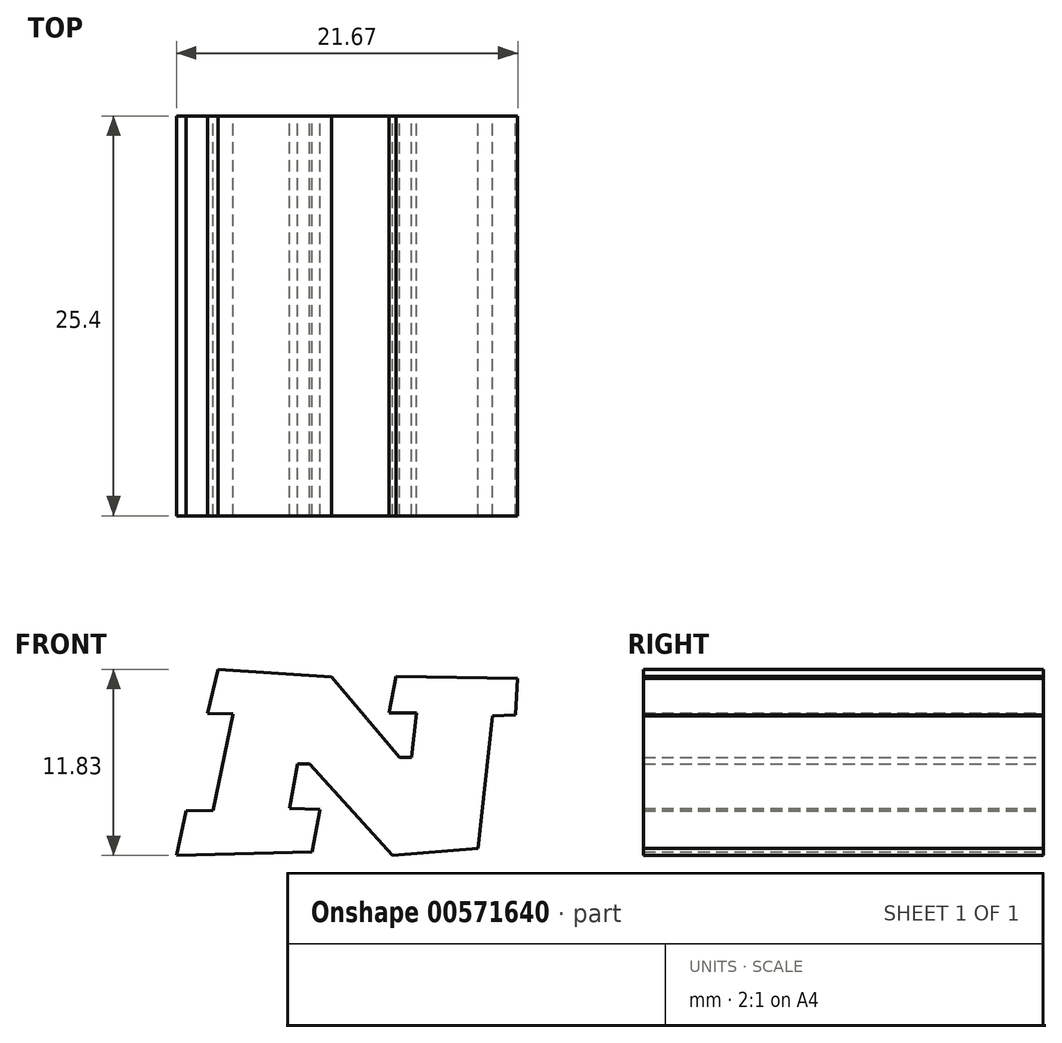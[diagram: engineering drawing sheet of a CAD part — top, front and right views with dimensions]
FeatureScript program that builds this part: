
annotation { "Feature Type Name" : "Feature", "Feature Type Description" : "" }
export const myFeature = defineFeature(function(context is Context, id is Id, definition is map)
    precondition{}
    {
        {
            var Q0;
            Q0=qCreatedBy(makeId("Front.planeOp"),FACE);
            var sketch = newSketch(context, id + "F0", { "sketchPlane" : qUnion([Q0])});
            skFitSpline(sketch, "E0", {"points": [v(-58.4, 49.98) * mm, v(-60.28, 49.9) * mm, v(-62.5, 51.34) * mm, v(-63.35, 53.39) * mm, v(-63.35, 56.37) * mm, v(-62.67, 59.19) * mm, v(-61.05, 62.26) * mm, v(-58.92, 64.47) * mm, v(-56.27, 66.35) * mm, v(-53.29, 67.46) * mm, v(-49.88, 67.88) * mm, v(-46.55, 67.88) * mm, v(-44.42, 67.46) * mm, v(-42.2, 66.1) * mm, v(-40.24, 64.39) * mm, v(-38.7, 62.6) * mm, v(-37.68, 60.38) * mm, v(-36.06, 58.33) * mm, v(-34.7, 56.2) * mm, v(-33.93, 54.15) * mm, v(-33.25, 50.91) * mm, v(-32.4, 53.64) * mm, v(-31.37, 56.46) * mm, v(-30.43, 59.1) * mm, v(-29.58, 61.23) * mm, v(-28.39, 63.1) * mm, v(-25.66, 64.9) * mm, v(-22.93, 65.07) * mm, v(-20.63, 65.15) * mm, v(-17.47, 64.9) * mm, v(-14.66, 63.7) * mm, v(-14.15, 60.64) * mm, v(-14.66, 59.19) * mm, v(-12.78, 58.84) * mm, v(-10.48, 56.88) * mm, v(-11.33, 53.56) * mm, v(-12.87, 49.2) * mm, v(-14.91, 43.5) * mm, v(-14.49, 43.5) * mm, v(-11.16, 44.86) * mm, v(-6.73, 45.29) * mm, v(-3.15, 44.69) * mm, v(-1.1, 43.58) * mm, v(1.03, 41.1) * mm, v(2.4, 38.3) * mm, v(2.74, 38.9) * mm, v(3.67, 41.53) * mm, v(5.12, 45.37) * mm, v(11.33, 58.89) * mm], "startDerivative": vector(-109.1, -22.32) * mm, "endDerivative": vector(157.1, 333.02) * mm});
            skFitSpline(sketch, "E1", {"points": [v(9.15, 54.27) * mm, v(9.8, 55.46) * mm, v(10.82, 57.18) * mm, v(12.5, 59.97) * mm, v(14.65, 63.06) * mm, v(17.43, 66.2) * mm, v(20.08, 68) * mm, v(22.91, 69.14) * mm, v(25.96, 69.71) * mm, v(29.37, 69.64) * mm, v(32.92, 68.7) * mm, v(35.28, 67.2) * mm, v(36.24, 65.83) * mm, v(36.87, 64.39) * mm, v(37.18, 62.64) * mm, v(38.47, 61.88) * mm, v(39.59, 60.43) * mm, v(40.27, 58.71) * mm, v(40.37, 55.21) * mm, v(39.94, 53.4) * mm, v(38.55, 49.76) * mm, v(37.52, 47.71) * mm, v(36.35, 45.4) * mm, v(36.59, 45.36) * mm, v(37.92, 45.3) * mm, v(39.85, 44.97) * mm, v(41.44, 44.4) * mm, v(43.55, 43) * mm, v(43.77, 43.1) * mm, v(44.76, 43.85) * mm, v(46.5, 44.76) * mm, v(48.74, 45.2) * mm, v(50.73, 45.09) * mm, v(52.45, 44.03) * mm, v(53.32, 42.47) * mm, v(53.56, 39.4) * mm, v(53.97, 39.41) * mm, v(55.66, 38.75) * mm, v(56.74, 37.12) * mm, v(56.92, 34.7) * mm, v(56.08, 31.7) * mm, v(54.87, 28.86) * mm, v(53.18, 24.76) * mm, v(53.73, 24.82) * mm, v(55.78, 25.3) * mm, v(58.8, 25.36) * mm, v(62.23, 24.46) * mm, v(65.12, 22.9) * mm, v(67.23, 20.48) * mm, v(68.44, 18.61) * mm, v(68.95, 16.93) * mm, v(70.23, 15.82) * mm, v(72.19, 12.41) * mm, v(72.87, 9.09) * mm, v(72.95, 2.44) * mm, v(71.67, -3.28) * mm, v(68.99, -8.5) * mm, v(66.68, -11.44) * mm, v(64.72, -13.53) * mm, v(56.88, -18.9) * mm, v(51.51, -20.88) * mm, v(46.03, -22.2) * mm, v(39.34, -23.11) * mm, v(31.89, -23.82) * mm, v(13.7, -24.56) * mm, v(1.77, -25.4) * mm, v(-17.72, -27.26) * mm, v(-35.46, -30.33) * mm, v(-53.03, -34.33) * mm, v(-62.82, -36.78) * mm, v(-66.48, -35.67) * mm, v(-66.37, -32.52) * mm, v(-66.93, -32.47) * mm, v(-69.62, -32.32) * mm, v(-71.2, -30.9) * mm, v(-71.65, -28.37) * mm, v(-70.63, -25.22) * mm, v(-68.66, -20.6) * mm, v(-65.87, -13.91) * mm, v(-60.27, -1.04) * mm, v(-58.65, 2.45) * mm, v(-55.58, 4.59) * mm, v(-50.42, 5.35) * mm, v(-43.1, 5.7) * mm, v(-36.61, 5.82) * mm, v(-29.32, 5.7) * mm, v(-19.9, 5.57) * mm, v(1.25, 3.91) * mm, v(12.53, 2.83) * mm, v(22.12, 2.04) * mm, v(30.27, 1.6) * mm, v(38.2, 1.43) * mm, v(45.2, 2.7) * mm, v(51.34, 4.41) * mm, v(55.86, 8.76) * mm, v(54.58, 8) * mm, v(50.23, 5.52) * mm, v(43.66, 4.33) * mm, v(40.42, 5.7) * mm, v(39.14, 8) * mm, v(37.6, 6.8) * mm, v(33.86, 4.76) * mm, v(28.65, 4.16) * mm, v(24.73, 6.38) * mm, v(23.2, 8.68) * mm, v(22, 8) * mm, v(16.97, 5.44) * mm, v(11.86, 4.33) * mm, v(7.25, 4.76) * mm, v(3.16, 8.68) * mm, v(2.48, 8.25) * mm, v(-1.53, 6.03) * mm, v(-5.71, 4.67) * mm], "startDerivative": vector(118.95, 221.72) * mm, "endDerivative": vector(-425.56, -118.04) * mm});
            skFitSpline(sketch, "E2", {"points": [v(-25.4, 6.03) * mm, v(-24.27, 6.45) * mm, v(-22.56, 7.45) * mm, v(-20.6, 8.96) * mm, v(-20.45, 8.84) * mm, v(-19.72, 8) * mm, v(-18.28, 6.85) * mm, v(-15.81, 5.34) * mm], "startDerivative": vector(8.64, 3.07) * mm, "endDerivative": vector(13.18, -8.38) * mm});
            skFitSpline(sketch, "E3", {"points": [v(-25.4, 6.03) * mm, v(-25.4, 5.69) * mm], "startDerivative": vector(0, -0.34) * mm, "endDerivative": vector(0, -0.34) * mm});
            skFitSpline(sketch, "E4", {"points": [v(-42.66, 6.03) * mm, v(-41.59, 6.58) * mm, v(-39.9, 7.7) * mm, v(-38.56, 8.62) * mm, v(-38.48, 8.43) * mm, v(-37.62, 7.31) * mm, v(-36.44, 6.03) * mm, v(-36.42, 5.82) * mm], "startDerivative": vector(6.87, 3.3) * mm, "endDerivative": vector(-0.7, -3.13) * mm});
            skFitSpline(sketch, "E5", {"points": [v(-42.66, 6.04) * mm, v(-42.66, 5.82) * mm, v(-42.66, 5.71) * mm], "startDerivative": vector(0, -0.32) * mm, "endDerivative": vector(0, -0.24) * mm});
            skFitSpline(sketch, "E6", {"points": [v(-53.48, 5.28) * mm, v(-54.72, 6.03) * mm, v(-56.42, 7.6) * mm, v(-57.8, 9.4) * mm, v(-58.54, 9.76) * mm, v(-60.31, 11.28) * mm, v(-61.91, 12.9) * mm, v(-63.15, 14.8) * mm, v(-63.81, 16.88) * mm, v(-64.22, 19.11) * mm, v(-64.12, 22.7) * mm, v(-63.36, 25.85) * mm, v(-62.72, 28.38) * mm, v(-61.73, 31.07) * mm, v(-60.92, 33.5) * mm, v(-55.8, 45.72) * mm, v(-56.22, 45.89) * mm, v(-58.01, 47.3) * mm, v(-58.4, 49.98) * mm], "startDerivative": vector(-28.66, 16) * mm, "endDerivative": vector(1.9, 49.58) * mm});
            skFitSpline(sketch, "E7", {"points": [v(16.22, 39.93) * mm, v(17.3, 41.18) * mm, v(18.94, 43.5) * mm, v(20.77, 45.91) * mm, v(22.35, 48.31) * mm, v(25.07, 52.98) * mm, v(27.26, 57) * mm, v(28.55, 59.21) * mm, v(28.98, 61.47) * mm, v(28.48, 61.22) * mm, v(26.9, 59.54) * mm, v(24.64, 56.42) * mm, v(22.78, 53.55) * mm, v(21.02, 50.54) * mm, v(18.83, 46.16) * mm, v(16.22, 39.93) * mm]});
            skFitSpline(sketch, "E8", {"points": [v(30.45, 19.02) * mm, v(31.23, 19.2) * mm, v(32.92, 20.95) * mm, v(34.37, 23.54) * mm, v(35.63, 26.43) * mm, v(36.9, 29.27) * mm, v(38.2, 33.3) * mm, v(38.77, 36.44) * mm, v(37.38, 37.29) * mm, v(35.15, 36.32) * mm, v(33.58, 34.7) * mm, v(31.9, 33) * mm, v(30.63, 30.72) * mm, v(29.24, 28.38) * mm, v(28.46, 25.1) * mm, v(28.28, 22.76) * mm, v(29.48, 19.38) * mm, v(30.45, 19.02) * mm]});
            skFitSpline(sketch, "E9", {"points": [v(-59.75, 51.85) * mm, v(-60.76, 52.42) * mm, v(-61.37, 53.68) * mm, v(-61.33, 55.54) * mm, v(-60.58, 58.41) * mm, v(-59.54, 60.74) * mm, v(-57.64, 62.82) * mm, v(-55.13, 64.65) * mm, v(-52.05, 65.69) * mm, v(-48.68, 66.01) * mm, v(-45.92, 65.69) * mm, v(-43.26, 64.54) * mm, v(-41.07, 62.64) * mm, v(-39.57, 60.06) * mm, v(-38.85, 57.62) * mm, v(-38.92, 54.07) * mm, v(-39.93, 50.6) * mm, v(-41, 47.58) * mm, v(-42.35, 44.22) * mm, v(-48.08, 30.43) * mm, v(-49.36, 27.36) * mm, v(-50.12, 24.12) * mm, v(-49.95, 20.02) * mm, v(-48.08, 18.57) * mm, v(-45.1, 18.66) * mm, v(-42.79, 21.73) * mm, v(-39.63, 27.87) * mm, v(-37.25, 34.1) * mm, v(-35.29, 39.41) * mm, v(-31.96, 49.1) * mm, v(-28.04, 59.5) * mm, v(-26.33, 62.06) * mm, v(-22.58, 63.17) * mm, v(-19.08, 63) * mm, v(-16.61, 62.49) * mm, v(-16.18, 60.78) * mm, v(-17.55, 56.26) * mm, v(-19.5, 51.23) * mm, v(-21.13, 46.29) * mm, v(-23.1, 40.92) * mm, v(-25.05, 36.32) * mm, v(-27.78, 29.23) * mm, v(-29.4, 25.14) * mm, v(-30.77, 21.81) * mm, v(-31.1, 19) * mm, v(-29.32, 18.66) * mm, v(-27.36, 20.02) * mm, v(-25.73, 22.07) * mm, v(-25.22, 25.9) * mm, v(-23.18, 31.02) * mm, v(-21.22, 34.95) * mm, v(-18.15, 38.53) * mm, v(-15.16, 40.92) * mm, v(-10.73, 42.88) * mm, v(-7.4, 43.47) * mm, v(-3.73, 42.8) * mm, v(0, 39.41) * mm, v(0, 34.95) * mm, v(-1.77, 31.2) * mm, v(-4.93, 29.66) * mm, v(-8.22, 30.18) * mm, v(-9.26, 31) * mm, v(-10.01, 32.58) * mm, v(-9.87, 33.87) * mm, v(-9.26, 35.09) * mm, v(-8.43, 35.99) * mm, v(-7.47, 36.32) * mm, v(-6.68, 36.32) * mm, v(-5.35, 36.32) * mm, v(-5.53, 37.06) * mm, v(-6, 37.67) * mm, v(-7.44, 38.08) * mm, v(-9.11, 37.55) * mm, v(-11.52, 35.9) * mm, v(-12.74, 34.46) * mm, v(-13.86, 32.78) * mm, v(-16.05, 27.87) * mm, v(-16.31, 25.1) * mm, v(-16.01, 21.82) * mm, v(-14.9, 19.86) * mm, v(-12.18, 18.57) * mm, v(-9.17, 18.46) * mm, v(-6.77, 19.2) * mm, v(-4.3, 20.07) * mm, v(-0.6, 22.22) * mm, v(0.5, 25.77) * mm, v(1.51, 29.14) * mm, v(2.73, 32.76) * mm, v(3.95, 36.32) * mm, v(5.25, 40.24) * mm, v(8.27, 47.95) * mm, v(10.24, 52.16) * mm, v(13.08, 57.08) * mm, v(16.12, 61.64) * mm, v(18.98, 64.84) * mm, v(22.68, 66.97) * mm, v(26.18, 67.73) * mm, v(29.78, 67.42) * mm, v(33.22, 66.3) * mm, v(35.15, 63.26) * mm, v(34.54, 58.35) * mm, v(32.87, 54.44) * mm, v(31.23, 51.45) * mm, v(29.93, 48.76) * mm, v(28.3, 46.13) * mm, v(21.52, 36.95) * mm, v(19.23, 34.66) * mm, v(16.63, 31.88) * mm, v(13.7, 28.8) * mm, v(10.48, 25.85) * mm, v(10.42, 25.13) * mm, v(9.52, 22.12) * mm, v(9.7, 19.2) * mm, v(11.27, 18.26) * mm, v(14.76, 19.2) * mm, v(18.74, 21.75) * mm, v(18.86, 22.48) * mm, v(18.92, 24.47) * mm, v(19.29, 26.64) * mm, v(20.25, 28.99) * mm, v(21.82, 33.21) * mm, v(23.8, 36.32) * mm, v(26.28, 38.76) * mm, v(29.48, 41.17) * mm, v(32.85, 42.68) * mm, v(35.69, 43.34) * mm, v(37.92, 43.34) * mm, v(40.45, 42.74) * mm, v(43.35, 39.96) * mm, v(43.83, 40.5) * mm, v(45.82, 42.13) * mm, v(47.69, 42.86) * mm, v(49.8, 43.22) * mm, v(51.55, 42.01) * mm, v(51.67, 40.02) * mm, v(51, 37.67) * mm, v(49.86, 35.02) * mm, v(48.65, 31.7) * mm, v(47.32, 28.63) * mm, v(45.46, 23.62) * mm, v(44.43, 20.55) * mm, v(44.5, 19.2) * mm, v(45.58, 18.02) * mm, v(48.23, 19.2) * mm, v(51.24, 21.63) * mm, v(54.98, 23.08) * mm, v(58.54, 23.38) * mm, v(62.16, 22.36) * mm, v(65.35, 19.95) * mm, v(67.1, 16.63) * mm, v(67.73, 11.37) * mm, v(67.51, 6.85) * mm, v(66.68, 2.73) * mm, v(64.36, -1.93) * mm, v(60.99, -6.52) * mm, v(55.9, -10.68) * mm, v(51.38, -13.19) * mm, v(45.94, -15.13) * mm, v(41.12, -16.16) * mm, v(35.15, -16.92) * mm, v(30.85, -17.3) * mm, v(25.56, -17.7) * mm, v(4.96, -18.64) * mm, v(-3.82, -19.28) * mm, v(-8.98, -19.71) * mm, v(-35.46, -23.11) * mm, v(-48.27, -25.9) * mm, v(-57.09, -28.13) * mm, v(-65.2, -30.33) * mm, v(-67.62, -30.33) * mm, v(-69.49, -29.84) * mm, v(-69.56, -28.05) * mm, v(-68.48, -25.43) * mm, v(-67.3, -22.57) * mm, v(-65.94, -19.2) * mm, v(-64.58, -16.18) * mm, v(-63.18, -12.6) * mm, v(-61.24, -8.5) * mm, v(-58.65, -2.15) * mm, v(-57.18, 1.05) * mm, v(-55.8, 2.45) * mm, v(-53.63, 3.23) * mm, v(-50.6, 3.58) * mm, v(-46.43, 3.74) * mm, v(-42.58, 3.89) * mm, v(-23.57, 3.89) * mm, v(-19.5, 3.58) * mm, v(-15, 3.33) * mm, v(-3.7, 2.45) * mm, v(2.9, 1.71) * mm, v(9.96, 1.1) * mm, v(25.18, 0) * mm, v(32.94, -0.43) * mm, v(40.96, 0) * mm, v(46.41, 1.15) * mm, v(53.01, 3.2) * mm, v(55.67, 5.32) * mm, v(58.21, 8.73) * mm, v(59.32, 12.17) * mm, v(59.29, 15.11) * mm, v(58.4, 17.2) * mm, v(56.35, 17.94) * mm, v(53.97, 17.08) * mm, v(52.05, 15.69) * mm, v(48.9, 13.28) * mm, v(46.27, 11.92) * mm, v(43.33, 10.88) * mm, v(40.4, 10.45) * mm, v(37.96, 10.92) * mm, v(36.45, 12.5) * mm, v(36.06, 14) * mm, v(35.91, 15.65) * mm, v(35.7, 15.4) * mm, v(33.94, 13.93) * mm, v(31.89, 12.39) * mm, v(28.56, 10.77) * mm, v(25.37, 10.38) * mm, v(22.43, 11.31) * mm, v(20.68, 13) * mm, v(20, 14.54) * mm, v(19.82, 15.61) * mm, v(19.39, 15.31) * mm, v(17.39, 14.08) * mm, v(14.32, 12.2) * mm, v(10.99, 11.1) * mm, v(6.73, 10.37) * mm, v(4.16, 10.65) * mm, v(1.9, 11.83) * mm, v(-0.48, 15.57) * mm, v(-0.9, 15.32) * mm, v(-5.6, 12.48) * mm, v(-8.96, 11.08) * mm, v(-12.04, 10.54) * mm, v(-16.42, 10.5) * mm, v(-20, 11.76) * mm, v(-23.09, 13.87) * mm, v(-24.6, 15.6) * mm, v(-24.99, 15.3) * mm, v(-27.25, 13.62) * mm, v(-31.18, 11.45) * mm, v(-34.27, 10.62) * mm, v(-37.9, 10.8) * mm, v(-39.78, 11.78) * mm, v(-41.02, 13.07) * mm, v(-42.11, 15.5) * mm, v(-42.5, 15.4) * mm, v(-43.47, 14.57) * mm, v(-45.08, 13.35) * mm, v(-46.85, 12.3) * mm, v(-49.03, 11.28) * mm, v(-51.42, 10.54) * mm, v(-53.83, 10.4) * mm, v(-55.8, 10.6) * mm, v(-58.42, 12.08) * mm, v(-60.68, 14.4) * mm, v(-61.86, 16.78) * mm, v(-62.25, 20.04) * mm, v(-61.73, 24.26) * mm, v(-61.15, 26.85) * mm, v(-60.23, 29.63) * mm, v(-56.54, 39.41) * mm, v(-53.53, 46.04) * mm, v(-50.6, 52.68) * mm, v(-49.3, 56.9) * mm, v(-49.37, 58.87) * mm, v(-51.2, 60.27) * mm, v(-53.64, 60.05) * mm, v(-55.22, 58.48) * mm, v(-56.3, 56.15) * mm, v(-56.97, 53.57) * mm, v(-57.51, 52.35) * mm, v(-59.75, 51.85) * mm]});
            skFitSpline(sketch, "E10", {"points": [v(-60.27, -25.66) * mm, v(-53.57, -23.82) * mm, v(-46.98, -22.32) * mm], "startDerivative": vector(13.3, 3.82) * mm, "endDerivative": vector(13.26, 2.87) * mm});
            skLineSegment(sketch, "E11", {"start": v(-46.98, -22.32) * mm, "end": v(-41.88, -17.6) * mm});
            skLineSegment(sketch, "E12", {"start": v(-41.88, -17.6) * mm, "end": v(-40.26, -11.71) * mm});
            skLineSegment(sketch, "E13", {"start": v(-40.26, -11.71) * mm, "end": v(-40.82, -10.5) * mm});
            skLineSegment(sketch, "E14", {"start": v(-40.82, -10.5) * mm, "end": v(-39.4, -9.23) * mm});
            skLineSegment(sketch, "E15", {"start": v(-39.4, -9.23) * mm, "end": v(-37.83, -3.6) * mm});
            skLineSegment(sketch, "E16", {"start": v(-37.83, -3.6) * mm, "end": v(-40.46, -0.15) * mm});
            skLineSegment(sketch, "E17", {"start": v(-40.46, -0.15) * mm, "end": v(-53.24, -0.81) * mm});
            skLineSegment(sketch, "E18", {"start": v(-53.24, -0.81) * mm, "end": v(-54.96, -7.1) * mm});
            skLineSegment(sketch, "E19", {"start": v(-54.96, -7.1) * mm, "end": v(-53.6, -7) * mm});
            skLineSegment(sketch, "E20", {"start": v(-53.6, -7) * mm, "end": v(-57, -19.32) * mm});
            skLineSegment(sketch, "E21", {"start": v(-57, -19.32) * mm, "end": v(-58.56, -19.72) * mm});
            skLineSegment(sketch, "E22", {"start": v(-58.56, -19.72) * mm, "end": v(-60.24, -25.6) * mm});
            skLineSegment(sketch, "E23", {"start": v(-47.51, -6.03) * mm, "end": v(-48.37, -9.03) * mm});
            skLineSegment(sketch, "E24", {"start": v(-48.37, -9.03) * mm, "end": v(-45.33, -8.72) * mm});
            skLineSegment(sketch, "E25", {"start": v(-45.33, -8.72) * mm, "end": v(-44.47, -5.98) * mm});
            skLineSegment(sketch, "E26", {"start": v(-44.47, -5.98) * mm, "end": v(-47.4, -6.09) * mm});
            skLineSegment(sketch, "E27", {"start": v(-50.8, -17.88) * mm, "end": v(-47.56, -17.22) * mm});
            skLineSegment(sketch, "E28", {"start": v(-47.56, -17.22) * mm, "end": v(-46.67, -13.97) * mm});
            skLineSegment(sketch, "E29", {"start": v(-46.67, -13.97) * mm, "end": v(-49.9, -14.5) * mm});
            skLineSegment(sketch, "E30", {"start": v(-49.9, -14.5) * mm, "end": v(-50.8, -17.83) * mm});
            skLineSegment(sketch, "E31", {"start": v(-39.5, -15.87) * mm, "end": v(-37.8, -15.7) * mm});
            skLineSegment(sketch, "E32", {"start": v(-37.8, -15.7) * mm, "end": v(-34.85, -5.04) * mm});
            skLineSegment(sketch, "E33", {"start": v(-34.85, -5.04) * mm, "end": v(-36.38, -5.13) * mm});
            skLineSegment(sketch, "E34", {"start": v(-36.38, -5.13) * mm, "end": v(-34.98, -0.18) * mm});
            skLineSegment(sketch, "E35", {"start": v(-34.98, -0.18) * mm, "end": v(-22.19, -0.1) * mm});
            skLineSegment(sketch, "E36", {"start": v(-22.19, -0.1) * mm, "end": v(-19.42, -3.3) * mm});
            skLineSegment(sketch, "E37", {"start": v(-19.42, -3.3) * mm, "end": v(-20.78, -7.98) * mm});
            skLineSegment(sketch, "E38", {"start": v(-20.78, -7.98) * mm, "end": v(-23.72, -10.29) * mm});
            skLineSegment(sketch, "E39", {"start": v(-23.72, -10.29) * mm, "end": v(-22.53, -13.87) * mm});
            skLineSegment(sketch, "E40", {"start": v(-22.53, -13.87) * mm, "end": v(-20.78, -13.74) * mm});
            skLineSegment(sketch, "E41", {"start": v(-20.78, -13.74) * mm, "end": v(-21.93, -17.96) * mm});
            skLineSegment(sketch, "E42", {"start": v(-21.93, -17.96) * mm, "end": v(-30.29, -19.03) * mm});
            skLineSegment(sketch, "E43", {"start": v(-30.29, -19.03) * mm, "end": v(-29.14, -14.76) * mm});
            skLineSegment(sketch, "E44", {"start": v(-29.14, -14.76) * mm, "end": v(-28.33, -14.68) * mm});
            skLineSegment(sketch, "E45", {"start": v(-28.33, -14.68) * mm, "end": v(-29.14, -11.86) * mm});
            skLineSegment(sketch, "E46", {"start": v(-29.14, -11.86) * mm, "end": v(-30.93, -12.03) * mm});
            skLineSegment(sketch, "E47", {"start": v(-30.93, -12.03) * mm, "end": v(-31.82, -15.15) * mm});
            skLineSegment(sketch, "E48", {"start": v(-31.82, -15.15) * mm, "end": v(-30.93, -15.1) * mm});
            skLineSegment(sketch, "E49", {"start": v(-30.93, -15.1) * mm, "end": v(-32.04, -19.28) * mm});
            skLineSegment(sketch, "E50", {"start": v(-32.04, -19.28) * mm, "end": v(-40.86, -20.9) * mm});
            skLineSegment(sketch, "E51", {"start": v(-40.86, -20.9) * mm, "end": v(-39.45, -15.91) * mm});
            skLineSegment(sketch, "E52", {"start": v(-28.86, -4.73) * mm, "end": v(-25.77, -4.73) * mm});
            skLineSegment(sketch, "E53", {"start": v(-25.77, -4.73) * mm, "end": v(-26.43, -7.18) * mm});
            skLineSegment(sketch, "E54", {"start": v(-26.43, -7.18) * mm, "end": v(-29.67, -7.25) * mm});
            skLineSegment(sketch, "E55", {"start": v(-29.67, -7.25) * mm, "end": v(-28.9, -4.73) * mm});
            skLineSegment(sketch, "E56", {"start": v(-16.84, -4.78) * mm, "end": v(-15.73, -0.6) * mm});
            skLineSegment(sketch, "E57", {"start": v(-15.73, -0.6) * mm, "end": v(-7.97, -1.11) * mm});
            skLineSegment(sketch, "E58", {"start": v(-7.97, -1.11) * mm, "end": v(-8.75, -4.5) * mm});
            skLineSegment(sketch, "E59", {"start": v(-8.75, -4.5) * mm, "end": v(-9.57, -4.5) * mm});
            skLineSegment(sketch, "E60", {"start": v(-9.57, -4.5) * mm, "end": v(-11.9, -12.76) * mm});
            skLineSegment(sketch, "E61", {"start": v(-11.9, -12.76) * mm, "end": v(-8.55, -12.64) * mm});
            skLineSegment(sketch, "E62", {"start": v(-8.55, -12.64) * mm, "end": v(-6.34, -4.75) * mm});
            skLineSegment(sketch, "E63", {"start": v(-6.34, -4.75) * mm, "end": v(-7.25, -4.65) * mm});
            skLineSegment(sketch, "E64", {"start": v(-7.25, -4.65) * mm, "end": v(-6.36, -1.36) * mm});
            skLineSegment(sketch, "E65", {"start": v(-6.36, -1.36) * mm, "end": v(2.13, -2.12) * mm});
            skLineSegment(sketch, "E66", {"start": v(2.13, -2.12) * mm, "end": v(1.34, -5.36) * mm});
            skLineSegment(sketch, "E67", {"start": v(1.34, -5.36) * mm, "end": v(-0.36, -5.18) * mm});
            skLineSegment(sketch, "E68", {"start": v(-0.36, -5.18) * mm, "end": v(-2.49, -13.35) * mm});
            skLineSegment(sketch, "E69", {"start": v(-2.49, -13.35) * mm, "end": v(-7, -16.21) * mm});
            skLineSegment(sketch, "E70", {"start": v(-7, -16.21) * mm, "end": v(-15.34, -17.15) * mm});
            skLineSegment(sketch, "E71", {"start": v(-15.34, -17.15) * mm, "end": v(-18.2, -14.49) * mm});
            skLineSegment(sketch, "E72", {"start": v(-18.2, -14.49) * mm, "end": v(-15.6, -4.7) * mm});
            skLineSegment(sketch, "E73", {"start": v(-15.6, -4.7) * mm, "end": v(-16.84, -4.78) * mm});
            skLineSegment(sketch, "E74", {"start": v(4.66, -5.5) * mm, "end": v(3.04, -12.26) * mm});
            skLineSegment(sketch, "E75", {"start": v(3.04, -12.26) * mm, "end": v(1.53, -12.38) * mm});
            skLineSegment(sketch, "E76", {"start": v(1.53, -12.38) * mm, "end": v(0.44, -15.46) * mm});
            skLineSegment(sketch, "E77", {"start": v(0.44, -15.46) * mm, "end": v(10.15, -15.27) * mm});
            skLineSegment(sketch, "E78", {"start": v(10.15, -15.27) * mm, "end": v(10.88, -12.56) * mm});
            skLineSegment(sketch, "E79", {"start": v(10.88, -12.56) * mm, "end": v(9.49, -12.44) * mm});
            skLineSegment(sketch, "E80", {"start": v(9.49, -12.44) * mm, "end": v(10.82, -5.93) * mm});
            skLineSegment(sketch, "E81", {"start": v(10.82, -5.93) * mm, "end": v(12.32, -5.99) * mm});
            skLineSegment(sketch, "E82", {"start": v(12.32, -5.99) * mm, "end": v(13.05, -2.91) * mm});
            skLineSegment(sketch, "E83", {"start": v(13.05, -2.91) * mm, "end": v(3.88, -2.25) * mm});
            skLineSegment(sketch, "E84", {"start": v(3.88, -2.25) * mm, "end": v(3.1, -5.57) * mm});
            skLineSegment(sketch, "E85", {"start": v(3.1, -5.57) * mm, "end": v(4.79, -5.45) * mm});
            skLineSegment(sketch, "E86", {"start": v(14.97, -3.03) * mm, "end": v(22.17, -3.51) * mm});
            skLineSegment(sketch, "E87", {"start": v(22.17, -3.51) * mm, "end": v(26.5, -8.63) * mm});
            skLineSegment(sketch, "E88", {"start": v(26.5, -8.63) * mm, "end": v(27.24, -8.63) * mm});
            skLineSegment(sketch, "E89", {"start": v(27.24, -8.63) * mm, "end": v(27.56, -5.8) * mm});
            skLineSegment(sketch, "E90", {"start": v(27.56, -5.8) * mm, "end": v(25.82, -5.8) * mm});
            skLineSegment(sketch, "E91", {"start": v(25.82, -5.8) * mm, "end": v(26.27, -3.48) * mm});
            skLineSegment(sketch, "E92", {"start": v(26.27, -3.48) * mm, "end": v(34, -3.6) * mm});
            skLineSegment(sketch, "E93", {"start": v(34, -3.6) * mm, "end": v(33.85, -5.94) * mm});
            skLineSegment(sketch, "E94", {"start": v(33.85, -5.94) * mm, "end": v(32.4, -6) * mm});
            skLineSegment(sketch, "E95", {"start": v(32.4, -6) * mm, "end": v(31.48, -14.4) * mm});
            skLineSegment(sketch, "E96", {"start": v(31.48, -14.4) * mm, "end": v(26.06, -14.84) * mm});
            skLineSegment(sketch, "E97", {"start": v(26.06, -14.84) * mm, "end": v(20.77, -9.04) * mm});
            skLineSegment(sketch, "E98", {"start": v(20.77, -9.04) * mm, "end": v(20.03, -9.04) * mm});
            skLineSegment(sketch, "E99", {"start": v(20.03, -9.04) * mm, "end": v(19.52, -11.88) * mm});
            skLineSegment(sketch, "E100", {"start": v(19.52, -11.88) * mm, "end": v(21.43, -11.94) * mm});
            skLineSegment(sketch, "E101", {"start": v(21.43, -11.94) * mm, "end": v(20.94, -14.63) * mm});
            skLineSegment(sketch, "E102", {"start": v(20.94, -14.63) * mm, "end": v(12.33, -14.86) * mm});
            skLineSegment(sketch, "E103", {"start": v(12.33, -14.86) * mm, "end": v(12.93, -12.03) * mm});
            skLineSegment(sketch, "E104", {"start": v(12.93, -12.03) * mm, "end": v(14.63, -11.98) * mm});
            skLineSegment(sketch, "E105", {"start": v(14.63, -11.98) * mm, "end": v(15.93, -5.87) * mm});
            skLineSegment(sketch, "E106", {"start": v(15.93, -5.87) * mm, "end": v(14.31, -5.82) * mm});
            skLineSegment(sketch, "E107", {"start": v(14.31, -5.82) * mm, "end": v(14.97, -3) * mm});
            skLineSegment(sketch, "E108", {"start": v(41.1, -9.97) * mm, "end": v(35.3, -10.37) * mm});
            skLineSegment(sketch, "E109", {"start": v(35.3, -10.37) * mm, "end": v(35.06, -11.88) * mm});
            skLineSegment(sketch, "E110", {"start": v(35.06, -11.88) * mm, "end": v(38.45, -13.12) * mm});
            skLineSegment(sketch, "E111", {"start": v(38.45, -13.12) * mm, "end": v(47.22, -11.59) * mm});
            skLineSegment(sketch, "E112", {"start": v(47.22, -11.59) * mm, "end": v(50.07, -9.45) * mm});
            skLineSegment(sketch, "E113", {"start": v(50.07, -9.45) * mm, "end": v(50.8, -8.3) * mm});
            skLineSegment(sketch, "E114", {"start": v(50.8, -8.3) * mm, "end": v(50.78, -5.51) * mm});
            skLineSegment(sketch, "E115", {"start": v(50.78, -5.51) * mm, "end": v(48.67, -5.4) * mm});
            skLineSegment(sketch, "E116", {"start": v(48.67, -5.4) * mm, "end": v(41.48, -6.58) * mm});
            skLineSegment(sketch, "E117", {"start": v(41.48, -6.58) * mm, "end": v(41.46, -4.79) * mm});
            skLineSegment(sketch, "E118", {"start": v(41.46, -4.79) * mm, "end": v(44.94, -4.23) * mm});
            skLineSegment(sketch, "E119", {"start": v(44.94, -4.23) * mm, "end": v(45.04, -4.83) * mm});
            skLineSegment(sketch, "E120", {"start": v(45.04, -4.83) * mm, "end": v(50.63, -3.27) * mm});
            skLineSegment(sketch, "E121", {"start": v(50.63, -3.27) * mm, "end": v(50.67, -2.27) * mm});
            skLineSegment(sketch, "E122", {"start": v(50.67, -2.27) * mm, "end": v(47.64, -1.78) * mm});
            skLineSegment(sketch, "E123", {"start": v(47.64, -1.78) * mm, "end": v(39.35, -2.89) * mm});
            skLineSegment(sketch, "E124", {"start": v(39.35, -2.89) * mm, "end": v(35.62, -4.7) * mm});
            skLineSegment(sketch, "E125", {"start": v(35.62, -4.7) * mm, "end": v(35.51, -7.86) * mm});
            skLineSegment(sketch, "E126", {"start": v(35.51, -7.86) * mm, "end": v(37.9, -8.86) * mm});
            skLineSegment(sketch, "E127", {"start": v(37.9, -8.86) * mm, "end": v(44.79, -7.96) * mm});
            skLineSegment(sketch, "E128", {"start": v(44.79, -7.96) * mm, "end": v(44.9, -10.03) * mm});
            skLineSegment(sketch, "E129", {"start": v(44.9, -10.03) * mm, "end": v(41.27, -10.7) * mm});
            skLineSegment(sketch, "E130", {"start": v(41.27, -10.7) * mm, "end": v(41.12, -10) * mm});
            skSolve(sketch);
        }
        {
            var Q0;
            {var subQ0=sQuery(id+"F0.wireOp",EDGE,"E87");Q0=makeQuery(id+"F0.imprint","IMPRINT",FACE,{"disambiguationData":[TD([[makeQuery(id+"F0.imprint","IMPRINT",EDGE,{"derivedFrom":subQ0}),-1.0]])]});}
            extrude(context, id + "F1", {"entities" : qUnion([Q0]), "depth" : 25.4 * mm, "offsetDistance" : 25.4 * mm});
        }
    });
